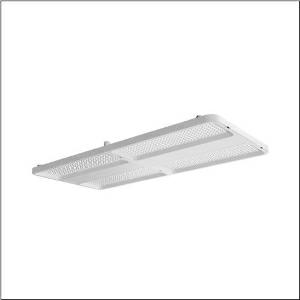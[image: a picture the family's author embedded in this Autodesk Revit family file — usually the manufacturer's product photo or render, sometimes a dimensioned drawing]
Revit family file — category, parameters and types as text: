
# Revit family: highbay_11_maxi_51hn11db4hda
name_source: partatom
category: Lighting Fixtures
units: mm (PartAtom-declared; Revit-internal decimal feet)

## family parameters
Cut with Voids When Loaded = No
Host = Face
Light Source = No
Part Type = Normal
Room Calculation Point = No
Round Connector Dimension = Use Diameter
Shared = No

## types (1)
- --- (1 x LED, 2990 lm, 15.1 W, 4000K)
    Apparent Load = 15 VA
    CIE Flux Codes = 85 97 100 100 100
    Color Rendering = 80
    Color Temperature = 4000K
    Default Elevation = 1800 mm
    Description = high bay luminaire Highbay 11 maxi; direct symmetric narrow distribution, light control with lens of PMMA; UGR ≤ 19 (X = 4H | Y = 8H | S = 0.25H | reflection values 70/50/20); luminous flux: 20.000lm; light colour: 840, colour temperature: 4000K, MacAdam ≤ 2 SDCM (initial), colour rendering: CRI > 80; luminous efficacy: 210,7lm/W; rated service life: 100.000h (L95/B50) at AT= 25°C; control: DALI 2; housing frame of high-performance plastic PA6, matt traffic white (RAL 9016); cover of PMMA; dimension (LxWxH): 946 x 442 x 72mm; luminaire connection: terminal, 5-pole, max. 2.5mm² (cable entry for one cable, Ø 8.5..16mm); mains connection: 230..240V, AC/DC 0/50..60Hz; connected load: 94,9W; protection rating (complete): IP66; insulation class (complete): insulation class I (protective earthing); protection symbol: D; impact resistance: IK08; halogen-free wiring; for central battery installations according to DIN EN 60598-2-22; corresponds to IFS (International Featured Standards) requirements for safety and quality in the food industry; LABS conformity tested according to VDMA 24364:2018-05; certification: CE, ENEC, VDE, UKCA; permissible operating ambient temperature: -40..+65°C (reducing of maximum allowable ambient temperature of 5°C with ceiling mounting); packaging unit: 1 piece; (delivery without accessories; please order mounting accessories separately)
    Height = 72 mm  [stored 0.23622 ft]
    Lamp = 1 x LED
    Lamp Light Flux = 2990 lm
    Lamp Power = 15.1 W
    Lamp count = 1
    Length = 946 mm
    Luminous efficacy = 198 lm/W
    Manufacturer = Siteco
    ModVariant = No
    Model = 51HN11DB4HDA
    Mounting Place = Ceiling
    Mounting Type = Pendant
    Number of Poles = 1
    OnlyDefault = Yes
    Power Factor = 1
    Product Name = Highbay 11 maxi
    Product group = high bay luminaire
    ProductGroupID = 901
    Protection Class = Protection class I
    Protection Degree = IP 66
    RLX_Detail_Level = 1
    RLX_Emergency_Light_Flux = 0 lm
    RLX_Emergency_Type = 0
    RLX_Emergency_Type_DB = No
    RlxData = <blob elided: 22249 chars, md5=ad1056b1>
    Socket = socket
    Standby Power = 0 W
    System Light Flux = 2990 lm
    System Power = 15 W
    Type Comments = : DC mode (central or group accumulator) initial emergency light level
    Type Image = l_1363244.jpg
    URL = http://relux.com
    VarID = @adj_003709
    Voltage = 0 V
    Weight = 0.00 kg
    Width = 442 mm

note: [stored X ft] marks values corroborated as IEEE doubles in the binary element streams (Revit-internal decimal feet)

## geometry (parser evidence)
native form markers: Blend x4, Sweep x11
no freeform markers — native parametric forms only
